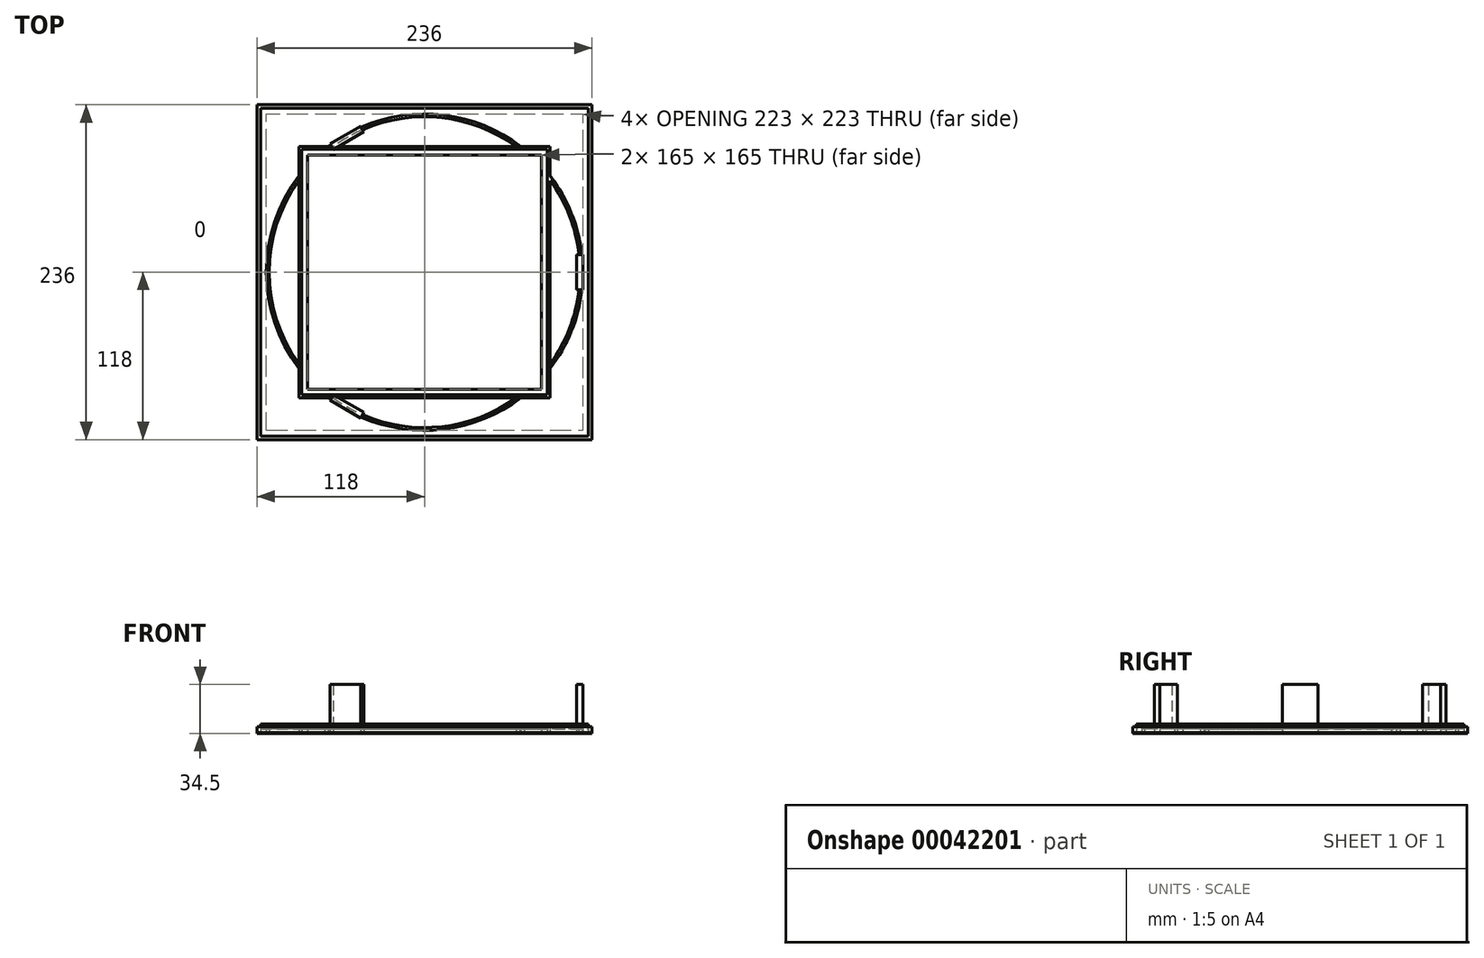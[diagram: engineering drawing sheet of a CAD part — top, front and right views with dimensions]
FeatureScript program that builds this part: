
annotation { "Feature Type Name" : "Feature", "Feature Type Description" : "" }
export const myFeature = defineFeature(function(context is Context, id is Id, definition is map)
    precondition{}
    {
        {
            var Q0;
            Q0=qCreatedBy(makeId("Top.planeOp"),FACE);
            var sketch = newSketch(context, id + "F0", { "sketchPlane" : qUnion([Q0])});
            skLineSegment(sketch, "E0.rect.bottom", {"start": v(118, 118) * mm, "end": v(-118, 118) * mm});
            skLineSegment(sketch, "E0.rect.top", {"start": v(118, -118) * mm, "end": v(-118, -118) * mm});
            skLineSegment(sketch, "E0.rect.left", {"start": v(118, 118) * mm, "end": v(118, -118) * mm});
            skLineSegment(sketch, "E0.rect.right", {"start": v(-118, 118) * mm, "end": v(-118, -118) * mm});
            skPoint(sketch, "E0.rect.middle", {"position": v(0, 0) * mm});
            skLineSegment(sketch, "E1.rect.bottom", {"start": v(-82.5, 82.5) * mm, "end": v(82.5, 82.5) * mm});
            skLineSegment(sketch, "E1.rect.top", {"start": v(-82.5, -82.5) * mm, "end": v(82.5, -82.5) * mm});
            skLineSegment(sketch, "E1.rect.left", {"start": v(-82.5, 82.5) * mm, "end": v(-82.5, -82.5) * mm});
            skLineSegment(sketch, "E1.rect.right", {"start": v(82.5, 82.5) * mm, "end": v(82.5, -82.5) * mm});
            skLineSegment(sketch, "E2.rect.bottom", {"start": v(-115.5, 115.5) * mm, "end": v(115.5, 115.5) * mm});
            skLineSegment(sketch, "E2.rect.top", {"start": v(-115.5, -115.5) * mm, "end": v(115.5, -115.5) * mm});
            skLineSegment(sketch, "E2.rect.left", {"start": v(-115.5, 115.5) * mm, "end": v(-115.5, -115.5) * mm});
            skLineSegment(sketch, "E2.rect.right", {"start": v(115.5, 115.5) * mm, "end": v(115.5, -115.5) * mm});
            skLineSegment(sketch, "E3.rect.bottom", {"start": v(-86.5, 86.5) * mm, "end": v(86.5, 86.5) * mm});
            skLineSegment(sketch, "E3.rect.top", {"start": v(-86.5, -86.5) * mm, "end": v(86.5, -86.5) * mm});
            skLineSegment(sketch, "E3.rect.left", {"start": v(-86.5, 86.5) * mm, "end": v(-86.5, -86.5) * mm});
            skLineSegment(sketch, "E3.rect.right", {"start": v(86.5, 86.5) * mm, "end": v(86.5, -86.5) * mm});
            skLineSegment(sketch, "E4.rect.bottom", {"start": v(-88.5, 88.5) * mm, "end": v(88.5, 88.5) * mm});
            skLineSegment(sketch, "E4.rect.top", {"start": v(-88.5, -88.5) * mm, "end": v(88.5, -88.5) * mm});
            skLineSegment(sketch, "E4.rect.left", {"start": v(-88.5, 88.5) * mm, "end": v(-88.5, -88.5) * mm});
            skLineSegment(sketch, "E4.rect.right", {"start": v(88.5, 88.5) * mm, "end": v(88.5, -88.5) * mm});
            skArc(sketch, "E5", {"start": v(70.36, 86.5) * mm, "mid": v(0, 111.5) * mm, "end": v(-70.36, 86.5) * mm});
            skArc(sketch, "E6", {"start": v(67.14, 86.5) * mm, "mid": v(0, 109.5) * mm, "end": v(-67.14, 86.5) * mm});
            skArc(sketch, "E7.trimOffspring", {"start": v(-86.5, 70.36) * mm, "mid": v(-111.5, 0) * mm, "end": v(-86.5, -70.36) * mm});
            skArc(sketch, "E8.trimOffspring", {"start": v(-86.5, 67.14) * mm, "mid": v(-109.5, 0) * mm, "end": v(-86.5, -67.14) * mm});
            skArc(sketch, "E9.trimOffspring", {"start": v(-67.14, -86.5) * mm, "mid": v(0, -109.5) * mm, "end": v(67.14, -86.5) * mm});
            skArc(sketch, "E10.trimOffspring", {"start": v(-70.36, -86.5) * mm, "mid": v(0, -111.5) * mm, "end": v(70.36, -86.5) * mm});
            skArc(sketch, "E11.trimOffspring", {"start": v(86.5, -67.14) * mm, "mid": v(109.5, 0) * mm, "end": v(86.5, 67.14) * mm});
            skArc(sketch, "E12.trimOffspring", {"start": v(86.5, -70.36) * mm, "mid": v(111.5, 0) * mm, "end": v(86.5, 70.36) * mm});
            skLineSegment(sketch, "E13", {"start": v(0, 0) * mm, "end": v(118, 0) * mm, "construction": true});
            skLineSegment(sketch, "E14.bottom", {"start": v(111.5, 0) * mm, "end": v(107, 0) * mm});
            skLineSegment(sketch, "E14.top", {"start": v(111.5, 12.5) * mm, "end": v(107, 12.5) * mm});
            skLineSegment(sketch, "E14.left", {"start": v(111.5, 0) * mm, "end": v(111.5, 12.5) * mm});
            skLineSegment(sketch, "E14.right", {"start": v(107, 0) * mm, "end": v(107, 12.5) * mm});
            skLineSegment(sketch, "E15.top", {"start": v(111.5, -12.5) * mm, "end": v(107, -12.5) * mm});
            skLineSegment(sketch, "E15.left", {"start": v(111.5, 0) * mm, "end": v(111.5, -12.5) * mm});
            skLineSegment(sketch, "E15.right", {"start": v(107, 0) * mm, "end": v(107, -12.5) * mm});
            skSolve(sketch);
        }
        {
            var Q0;
            Q0=makeQuery(id+"F0.imprint","IMPRINT",FACE,{"disambiguationData":[TD([[makeQuery(id+"F0.imprint","IMPRINT",EDGE,{"derivedFrom":sQuery(id+"F0.wireOp",EDGE,"E0.rect.bottom")}),1.0]])]});
            extrude(context, id + "F1", {"entities" : qUnion([Q0]), "depth" : 4 * mm});
        }
        {
            var Q0;
            Q0=makeQuery(id+"F0.imprint","IMPRINT",FACE,{"disambiguationData":[TD([[makeQuery(id+"F0.imprint","IMPRINT",EDGE,{"derivedFrom":sQuery(id+"F0.wireOp",EDGE,"E2.rect.bottom")}),-1.0]])]});
            extrude(context, id + "F2", {"entities" : qUnion([Q0]), "operationType" : NewBodyOperationType.ADD, "depth" : 2.5 * mm});
        }
        {
            var Q0;
            Q0=makeQuery(id+"F0.imprint","IMPRINT",FACE,{"disambiguationData":[TD([[makeQuery(id+"F0.imprint","IMPRINT",EDGE,{"derivedFrom":sQuery(id+"F0.wireOp",EDGE,"E1.rect.bottom")}),1.0]])]});
            extrude(context, id + "F3", {"entities" : qUnion([Q0]), "operationType" : NewBodyOperationType.ADD, "depth" : 2.5 * mm});
        }
        {
            var Q0;
            {var subQ1=sQuery(id+"F0.wireOp",EDGE,"E4.rect.top");var subQ4=sQuery(id+"F0.wireOp",EDGE,"E10.trimOffspring");var subQ6=makeQuery(id+"F0.imprint","INTERSECT",VERTEX,{"disambiguationData":[OD(0.0)],"derivedFrom":[subQ1,subQ4]});Q0=makeQuery(id+"F0.imprint","IMPRINT",FACE,{"disambiguationData":[TD([[makeQuery(id+"F0.imprint","IMPRINT",EDGE,{"disambiguationData":[TD([[subQ6,-1.0]])],"derivedFrom":subQ1}),-1.0]])]});}
            var Q1;
            {var subQ1=sQuery(id+"F0.wireOp",EDGE,"E9.trimOffspring");var subQ4=sQuery(id+"F0.wireOp",EDGE,"E3.rect.top");var subQ6=makeQuery(id+"F0.imprint","INTERSECT",VERTEX,{"disambiguationData":[OD(0.0)],"derivedFrom":[subQ4,subQ1]});Q1=makeQuery(id+"F0.imprint","IMPRINT",FACE,{"disambiguationData":[TD([[makeQuery(id+"F0.imprint","IMPRINT",EDGE,{"disambiguationData":[TD([[subQ6,-1.0]])],"derivedFrom":subQ4}),-1.0]])]});}
            var Q2;
            {var subQ3=sQuery(id+"F0.wireOp",EDGE,"E3.rect.top");var subQ5=sQuery(id+"F0.wireOp",EDGE,"E9.trimOffspring");var subQ7=makeQuery(id+"F0.imprint","INTERSECT",VERTEX,{"disambiguationData":[OD(0.0)],"derivedFrom":[subQ3,subQ5]});Q2=makeQuery(id+"F0.imprint","IMPRINT",FACE,{"disambiguationData":[TD([[makeQuery(id+"F0.imprint","IMPRINT",EDGE,{"disambiguationData":[TD([[subQ7,1.0]])],"derivedFrom":subQ3}),-1.0]])]});}
            var Q3;
            {var subQ3=sQuery(id+"F0.wireOp",EDGE,"E3.rect.top");var subQ5=sQuery(id+"F0.wireOp",EDGE,"E9.trimOffspring");var subQ7=makeQuery(id+"F0.imprint","INTERSECT",VERTEX,{"disambiguationData":[OD(1.0)],"derivedFrom":[subQ3,subQ5]});Q3=makeQuery(id+"F0.imprint","IMPRINT",FACE,{"disambiguationData":[TD([[makeQuery(id+"F0.imprint","IMPRINT",EDGE,{"disambiguationData":[TD([[subQ7,-1.0]])],"derivedFrom":subQ3}),-1.0]])]});}
            extrude(context, id + "F4", {"entities" : qUnion([Q0, Q1, Q2, Q3]), "depth" : 6 * mm});
        }
        {
            var Q0;
            {var subQ3=sQuery(id+"F0.wireOp",EDGE,"E11.trimOffspring");var subQ5=sQuery(id+"F0.wireOp",EDGE,"E4.rect.right");var subQ7=makeQuery(id+"F0.imprint","INTERSECT",VERTEX,{"disambiguationData":[OD(1.0)],"derivedFrom":[subQ5,subQ3]});Q0=makeQuery(id+"F0.imprint","IMPRINT",FACE,{"disambiguationData":[TD([[makeQuery(id+"F0.imprint","IMPRINT",EDGE,{"disambiguationData":[TD([[subQ7,-1.0]])],"derivedFrom":subQ5}),1.0]])]});}
            var Q1;
            {var subQ3=sQuery(id+"F0.wireOp",EDGE,"E3.rect.right");var subQ5=sQuery(id+"F0.wireOp",EDGE,"E11.trimOffspring");var subQ7=makeQuery(id+"F0.imprint","INTERSECT",VERTEX,{"disambiguationData":[OD(0.0)],"derivedFrom":[subQ3,subQ5]});Q1=makeQuery(id+"F0.imprint","IMPRINT",FACE,{"disambiguationData":[TD([[makeQuery(id+"F0.imprint","IMPRINT",EDGE,{"disambiguationData":[TD([[subQ7,-1.0]])],"derivedFrom":subQ3}),1.0]])]});}
            var Q2;
            {var subQ0=sQuery(id+"F0.wireOp",EDGE,"E11.trimOffspring");var subQ3=sQuery(id+"F0.wireOp",EDGE,"E3.rect.right");var subQ4=makeQuery(id+"F0.imprint","INTERSECT",VERTEX,{"disambiguationData":[OD(0.0)],"derivedFrom":[subQ3,subQ0]});Q2=makeQuery(id+"F0.imprint","IMPRINT",FACE,{"disambiguationData":[TD([[makeQuery(id+"F0.imprint","IMPRINT",EDGE,{"disambiguationData":[TD([[subQ4,1.0]])],"derivedFrom":subQ3}),1.0]])]});}
            var Q3;
            {var subQ3=sQuery(id+"F0.wireOp",EDGE,"E3.rect.right");var subQ5=sQuery(id+"F0.wireOp",EDGE,"E11.trimOffspring");var subQ7=makeQuery(id+"F0.imprint","INTERSECT",VERTEX,{"disambiguationData":[OD(1.0)],"derivedFrom":[subQ3,subQ5]});Q3=makeQuery(id+"F0.imprint","IMPRINT",FACE,{"disambiguationData":[TD([[makeQuery(id+"F0.imprint","IMPRINT",EDGE,{"disambiguationData":[TD([[subQ7,1.0]])],"derivedFrom":subQ3}),1.0]])]});}
            var Q4;
            {var subQ0=sQuery(id+"F0.wireOp",EDGE,"E12.trimOffspring");var subQ3=sQuery(id+"F0.wireOp",EDGE,"E4.rect.right");var subQ4=makeQuery(id+"F0.imprint","INTERSECT",VERTEX,{"disambiguationData":[OD(0.0)],"derivedFrom":[subQ3,subQ0]});Q4=makeQuery(id+"F0.imprint","IMPRINT",FACE,{"disambiguationData":[TD([[makeQuery(id+"F0.imprint","IMPRINT",EDGE,{"disambiguationData":[TD([[subQ4,-1.0]])],"derivedFrom":subQ3}),1.0]])]});}
            extrude(context, id + "F5", {"entities" : qUnion([Q0, Q1, Q2, Q3, Q4]), "depth" : 6 * mm});
        }
        {
            var Q0;
            {var subQ1=sQuery(id+"F0.wireOp",EDGE,"E4.rect.left");var subQ4=sQuery(id+"F0.wireOp",EDGE,"E7.trimOffspring");var subQ6=makeQuery(id+"F0.imprint","INTERSECT",VERTEX,{"disambiguationData":[OD(0.0)],"derivedFrom":[subQ1,subQ4]});Q0=makeQuery(id+"F0.imprint","IMPRINT",FACE,{"disambiguationData":[TD([[makeQuery(id+"F0.imprint","IMPRINT",EDGE,{"disambiguationData":[TD([[subQ6,-1.0]])],"derivedFrom":subQ1}),-1.0]])]});}
            var Q1;
            {var subQ3=sQuery(id+"F0.wireOp",EDGE,"E3.rect.left");var subQ5=sQuery(id+"F0.wireOp",EDGE,"E7.trimOffspring");var subQ7=makeQuery(id+"F0.imprint","INTERSECT",VERTEX,{"disambiguationData":[OD(1.0)],"derivedFrom":[subQ3,subQ5]});Q1=makeQuery(id+"F0.imprint","IMPRINT",FACE,{"disambiguationData":[TD([[makeQuery(id+"F0.imprint","IMPRINT",EDGE,{"disambiguationData":[TD([[subQ7,1.0]])],"derivedFrom":subQ3}),-1.0]])]});}
            var Q2;
            {var subQ0=sQuery(id+"F0.wireOp",EDGE,"E8.trimOffspring");var subQ3=sQuery(id+"F0.wireOp",EDGE,"E3.rect.left");var subQ6=makeQuery(id+"F0.imprint","INTERSECT",VERTEX,{"disambiguationData":[OD(0.0)],"derivedFrom":[subQ3,subQ0]});Q2=makeQuery(id+"F0.imprint","IMPRINT",FACE,{"disambiguationData":[TD([[makeQuery(id+"F0.imprint","IMPRINT",EDGE,{"disambiguationData":[TD([[subQ6,-1.0]])],"derivedFrom":subQ3}),-1.0]])]});}
            var Q3;
            {var subQ3=sQuery(id+"F0.wireOp",EDGE,"E3.rect.left");var subQ5=sQuery(id+"F0.wireOp",EDGE,"E7.trimOffspring");var subQ7=makeQuery(id+"F0.imprint","INTERSECT",VERTEX,{"disambiguationData":[OD(0.0)],"derivedFrom":[subQ3,subQ5]});Q3=makeQuery(id+"F0.imprint","IMPRINT",FACE,{"disambiguationData":[TD([[makeQuery(id+"F0.imprint","IMPRINT",EDGE,{"disambiguationData":[TD([[subQ7,-1.0]])],"derivedFrom":subQ3}),-1.0]])]});}
            extrude(context, id + "F6", {"entities" : qUnion([Q0, Q1, Q2, Q3]), "depth" : 6 * mm});
        }
        {
            var Q0;
            {var subQ0=sQuery(id+"F0.wireOp",EDGE,"E6");var subQ3=sQuery(id+"F0.wireOp",EDGE,"E3.rect.bottom");var subQ4=makeQuery(id+"F0.imprint","INTERSECT",VERTEX,{"disambiguationData":[OD(0.0)],"derivedFrom":[subQ3,subQ0]});Q0=makeQuery(id+"F0.imprint","IMPRINT",FACE,{"disambiguationData":[TD([[makeQuery(id+"F0.imprint","IMPRINT",EDGE,{"disambiguationData":[TD([[subQ4,1.0]])],"derivedFrom":subQ3}),1.0]])]});}
            var Q1;
            {var subQ0=sQuery(id+"F0.wireOp",EDGE,"E5");var subQ3=sQuery(id+"F0.wireOp",EDGE,"E3.rect.bottom");var subQ4=makeQuery(id+"F0.imprint","INTERSECT",VERTEX,{"disambiguationData":[OD(1.0)],"derivedFrom":[subQ3,subQ0]});Q1=makeQuery(id+"F0.imprint","IMPRINT",FACE,{"disambiguationData":[TD([[makeQuery(id+"F0.imprint","IMPRINT",EDGE,{"disambiguationData":[TD([[subQ4,-1.0]])],"derivedFrom":subQ3}),1.0]])]});}
            var Q2;
            {var subQ1=sQuery(id+"F0.wireOp",EDGE,"E4.rect.bottom");var subQ4=sQuery(id+"F0.wireOp",EDGE,"E5");var subQ6=makeQuery(id+"F0.imprint","INTERSECT",VERTEX,{"disambiguationData":[OD(0.0)],"derivedFrom":[subQ1,subQ4]});Q2=makeQuery(id+"F0.imprint","IMPRINT",FACE,{"disambiguationData":[TD([[makeQuery(id+"F0.imprint","IMPRINT",EDGE,{"disambiguationData":[TD([[subQ6,-1.0]])],"derivedFrom":subQ1}),1.0]])]});}
            var Q3;
            {var subQ3=sQuery(id+"F0.wireOp",EDGE,"E3.rect.bottom");var subQ5=sQuery(id+"F0.wireOp",EDGE,"E5");var subQ7=makeQuery(id+"F0.imprint","INTERSECT",VERTEX,{"disambiguationData":[OD(0.0)],"derivedFrom":[subQ3,subQ5]});Q3=makeQuery(id+"F0.imprint","IMPRINT",FACE,{"disambiguationData":[TD([[makeQuery(id+"F0.imprint","IMPRINT",EDGE,{"disambiguationData":[TD([[subQ7,1.0]])],"derivedFrom":subQ3}),1.0]])]});}
            extrude(context, id + "F7", {"entities" : qUnion([Q0, Q1, Q2, Q3]), "depth" : 6 * mm});
        }
        {
            var Q0;
            {var subQ3=sQuery(id+"F0.wireOp",EDGE,"E11.trimOffspring");var subQ5=sQuery(id+"F0.wireOp",EDGE,"E4.rect.right");var subQ7=makeQuery(id+"F0.imprint","INTERSECT",VERTEX,{"disambiguationData":[OD(1.0)],"derivedFrom":[subQ5,subQ3]});Q0=makeQuery(id+"F0.imprint","IMPRINT",FACE,{"disambiguationData":[TD([[makeQuery(id+"F0.imprint","IMPRINT",EDGE,{"disambiguationData":[TD([[subQ7,-1.0]])],"derivedFrom":subQ5}),1.0]])]});}
            extrude(context, id + "F8", {"entities" : qUnion([Q0]), "depth" : 6 * mm});
        }
        {
            var Q0;
            {var subQ0=sQuery(id+"F0.wireOp",EDGE,"E15.right");Q0=makeQuery(id+"F0.imprint","IMPRINT",FACE,{"disambiguationData":[TD([[makeQuery(id+"F0.imprint","IMPRINT",EDGE,{"derivedFrom":subQ0}),1.0]])]});}
            var Q1;
            {var subQ1=sQuery(id+"F0.wireOp",EDGE,"E11.trimOffspring");var subQ5=sQuery(id+"F0.wireOp",EDGE,"E15.top");var subQ7=makeQuery(id+"F0.imprint","INTERSECT",VERTEX,{"derivedFrom":[subQ1,subQ5]});Q1=makeQuery(id+"F0.imprint","IMPRINT",FACE,{"disambiguationData":[TD([[makeQuery(id+"F0.imprint","IMPRINT",EDGE,{"disambiguationData":[TD([[subQ7,-1.0]])],"derivedFrom":subQ1}),-1.0]])]});}
            var Q2;
            {var subQ3=sQuery(id+"F0.wireOp",EDGE,"E15.left");Q2=makeQuery(id+"F0.imprint","IMPRINT",FACE,{"disambiguationData":[TD([[makeQuery(id+"F0.imprint","IMPRINT",EDGE,{"derivedFrom":subQ3}),-1.0]])]});}
            var Q3;
            {var subQ0=sQuery(id+"F0.wireOp",EDGE,"E14.left");Q3=makeQuery(id+"F0.imprint","IMPRINT",FACE,{"disambiguationData":[TD([[makeQuery(id+"F0.imprint","IMPRINT",EDGE,{"derivedFrom":subQ0}),1.0]])]});}
            var Q4;
            {var subQ0=sQuery(id+"F0.wireOp",EDGE,"E14.bottom");var subQ1=sQuery(id+"F0.wireOp",EDGE,"E11.trimOffspring");var subQ2=makeQuery(id+"F0.imprint","INTERSECT",VERTEX,{"derivedFrom":[subQ1,subQ0]});Q4=makeQuery(id+"F0.imprint","IMPRINT",FACE,{"disambiguationData":[TD([[makeQuery(id+"F0.imprint","IMPRINT",EDGE,{"disambiguationData":[TD([[subQ2,-1.0]])],"derivedFrom":subQ1}),-1.0]])]});}
            var Q5;
            {var subQ0=sQuery(id+"F0.wireOp",EDGE,"E14.right");Q5=makeQuery(id+"F0.imprint","IMPRINT",FACE,{"disambiguationData":[TD([[makeQuery(id+"F0.imprint","IMPRINT",EDGE,{"derivedFrom":subQ0}),-1.0]])]});}
            extrude(context, id + "F9", {"entities" : qUnion([Q0, Q1, Q2, Q3, Q4, Q5]), "depth" : 34 * mm});
        }
        {
            var Q0;
            Q0=makeQuery(id+"F9.opExtrude","SWEPT_BODY",BODY,{"disambiguationData":[OSD([sQuery(id+"F0.wireOp",EDGE,"E14.top"),sQuery(id+"F0.wireOp",EDGE,"E14.left"),sQuery(id+"F0.wireOp",EDGE,"E14.right"),sQuery(id+"F0.wireOp",EDGE,"E15.top"),sQuery(id+"F0.wireOp",EDGE,"E15.left"),sQuery(id+"F0.wireOp",EDGE,"E15.right")])]});
            var Q1;
            Q1=sQuery(id+"F0.wireOp",EDGE,"E7.trimOffspring");
            circularPattern(context, id + "F10", {"entities" : qUnion([Q0]), "axis" : qUnion([Q1]), "angle" : 120 * degree, "instanceCount" : 3});
        }
        {
            var Q0;
            {var subQ0=sQuery(id+"F0.wireOp",EDGE,"E9.trimOffspring");var subQ1=sQuery(id+"F0.wireOp",EDGE,"E4.rect.top");var subQ3=makeQuery(id+"F0.imprint","INTERSECT",VERTEX,{"disambiguationData":[OD(0.0)],"derivedFrom":[subQ1,subQ0]});Q0=makeQuery(id+"F0.imprint","IMPRINT",FACE,{"disambiguationData":[TD([[makeQuery(id+"F0.imprint","IMPRINT",EDGE,{"disambiguationData":[TD([[subQ3,-1.0]])],"derivedFrom":subQ1}),-1.0]])]});}
            var Q1;
            {var subQ0=sQuery(id+"F0.wireOp",EDGE,"E8.trimOffspring");var subQ1=sQuery(id+"F0.wireOp",EDGE,"E4.rect.left");var subQ3=makeQuery(id+"F0.imprint","INTERSECT",VERTEX,{"disambiguationData":[OD(0.0)],"derivedFrom":[subQ1,subQ0]});Q1=makeQuery(id+"F0.imprint","IMPRINT",FACE,{"disambiguationData":[TD([[makeQuery(id+"F0.imprint","IMPRINT",EDGE,{"disambiguationData":[TD([[subQ3,-1.0]])],"derivedFrom":subQ1}),-1.0]])]});}
            var Q2;
            {var subQ4=sQuery(id+"F0.wireOp",EDGE,"E14.right");Q2=makeQuery(id+"F0.imprint","IMPRINT",FACE,{"disambiguationData":[TD([[makeQuery(id+"F0.imprint","IMPRINT",EDGE,{"derivedFrom":subQ4}),1.0]])]});}
            var Q3;
            {var subQ0=sQuery(id+"F0.wireOp",EDGE,"E6");var subQ1=sQuery(id+"F0.wireOp",EDGE,"E4.rect.bottom");var subQ3=makeQuery(id+"F0.imprint","INTERSECT",VERTEX,{"disambiguationData":[OD(0.0)],"derivedFrom":[subQ1,subQ0]});Q3=makeQuery(id+"F0.imprint","IMPRINT",FACE,{"disambiguationData":[TD([[makeQuery(id+"F0.imprint","IMPRINT",EDGE,{"disambiguationData":[TD([[subQ3,-1.0]])],"derivedFrom":subQ1}),1.0]])]});}
            extrude(context, id + "F11", {"entities" : qUnion([Q0, Q1, Q2, Q3]), "depth" : 2.5 * mm});
        }
        {
            var Q0;
            {var subQ0=sQuery(id+"F0.wireOp",EDGE,"E2.rect.bottom");var subQ1=sQuery(id+"F0.wireOp",EDGE,"E2.rect.top");var subQ2=sQuery(id+"F0.wireOp",EDGE,"E2.rect.left");var subQ3=sQuery(id+"F0.wireOp",EDGE,"E2.rect.right");Q0=makeQuery(id+"F2.boolean.opBoolean","MERGE",FACE,{"derivedFrom":[makeQuery(id+"F1.opExtrude","CAP_FACE",FACE,{"disambiguationData":[OSD([sQuery(id+"F0.wireOp",EDGE,"E0.rect.bottom"),sQuery(id+"F0.wireOp",EDGE,"E0.rect.top"),sQuery(id+"F0.wireOp",EDGE,"E0.rect.left"),sQuery(id+"F0.wireOp",EDGE,"E0.rect.right"),subQ0,subQ1,subQ2,subQ3])],"isStart":true}),makeQuery(id+"F2.opExtrude","CAP_FACE",FACE,{"disambiguationData":[OSD([subQ0,subQ1,subQ2,subQ3,sQuery(id+"F0.wireOp",EDGE,"E4.rect.bottom"),sQuery(id+"F0.wireOp",EDGE,"E4.rect.top"),sQuery(id+"F0.wireOp",EDGE,"E4.rect.left"),sQuery(id+"F0.wireOp",EDGE,"E4.rect.right"),sQuery(id+"F0.wireOp",EDGE,"E5"),sQuery(id+"F0.wireOp",EDGE,"E7.trimOffspring"),sQuery(id+"F0.wireOp",EDGE,"E10.trimOffspring"),sQuery(id+"F0.wireOp",EDGE,"E12.trimOffspring"),sQuery(id+"F0.wireOp",EDGE,"E14.top"),sQuery(id+"F0.wireOp",EDGE,"E14.left"),sQuery(id+"F0.wireOp",EDGE,"E15.top"),sQuery(id+"F0.wireOp",EDGE,"E15.left")])],"isStart":true})]});}
            var sketch = newSketch(context, id + "F12", { "sketchPlane" : qUnion([Q0])});
            skLineSegment(sketch, "E16.bottom", {"start": v(-118, 118) * mm, "end": v(118, 118) * mm});
            skLineSegment(sketch, "E16.top", {"start": v(-118, -118) * mm, "end": v(118, -118) * mm});
            skLineSegment(sketch, "E16.left", {"start": v(-118, 118) * mm, "end": v(-118, -118) * mm});
            skLineSegment(sketch, "E16.right", {"start": v(118, 118) * mm, "end": v(118, -118) * mm});
            skLineSegment(sketch, "E17.rect.bottom", {"start": v(82.5, -82.5) * mm, "end": v(-82.5, -82.5) * mm});
            skLineSegment(sketch, "E17.rect.top", {"start": v(82.5, 82.5) * mm, "end": v(-82.5, 82.5) * mm});
            skLineSegment(sketch, "E17.rect.left", {"start": v(82.5, -82.5) * mm, "end": v(82.5, 82.5) * mm});
            skLineSegment(sketch, "E17.rect.right", {"start": v(-82.5, -82.5) * mm, "end": v(-82.5, 82.5) * mm});
            skPoint(sketch, "E17.rect.middle", {"position": v(0, 0) * mm});
            skSolve(sketch);
        }
        {
            var Q0;
            Q0=makeQuery(id+"F12.imprint","IMPRINT",FACE,{"disambiguationData":[TD([[makeQuery(id+"F12.imprint","IMPRINT",EDGE,{"derivedFrom":sQuery(id+"F12.wireOp",EDGE,"E17.rect.bottom")}),1.0]])]});
            var Q1;
            Q1=makeQuery(id+"F12.imprint","IMPRINT",FACE,{"disambiguationData":[TD([[makeQuery(id+"F12.imprint","IMPRINT",EDGE,{"derivedFrom":sQuery(id+"F12.wireOp",EDGE,"E16.bottom")}),1.0]])]});
            extrude(context, id + "F13", {"entities" : qUnion([Q0, Q1]), "depth" : 0.5 * mm});
        }
        {
            var Q0;
            Q0=makeQuery(id+"F8.opExtrude","SWEPT_BODY",BODY,{"disambiguationData":[OSD([sQuery(id+"F0.wireOp",EDGE,"E4.rect.right"),sQuery(id+"F0.wireOp",EDGE,"E11.trimOffspring"),sQuery(id+"F0.wireOp",EDGE,"E12.trimOffspring"),sQuery(id+"F0.wireOp",EDGE,"E15.top")])]});
            deleteBodies(context, id + "F14", {"entities" : qUnion([Q0])});
        }
    });
